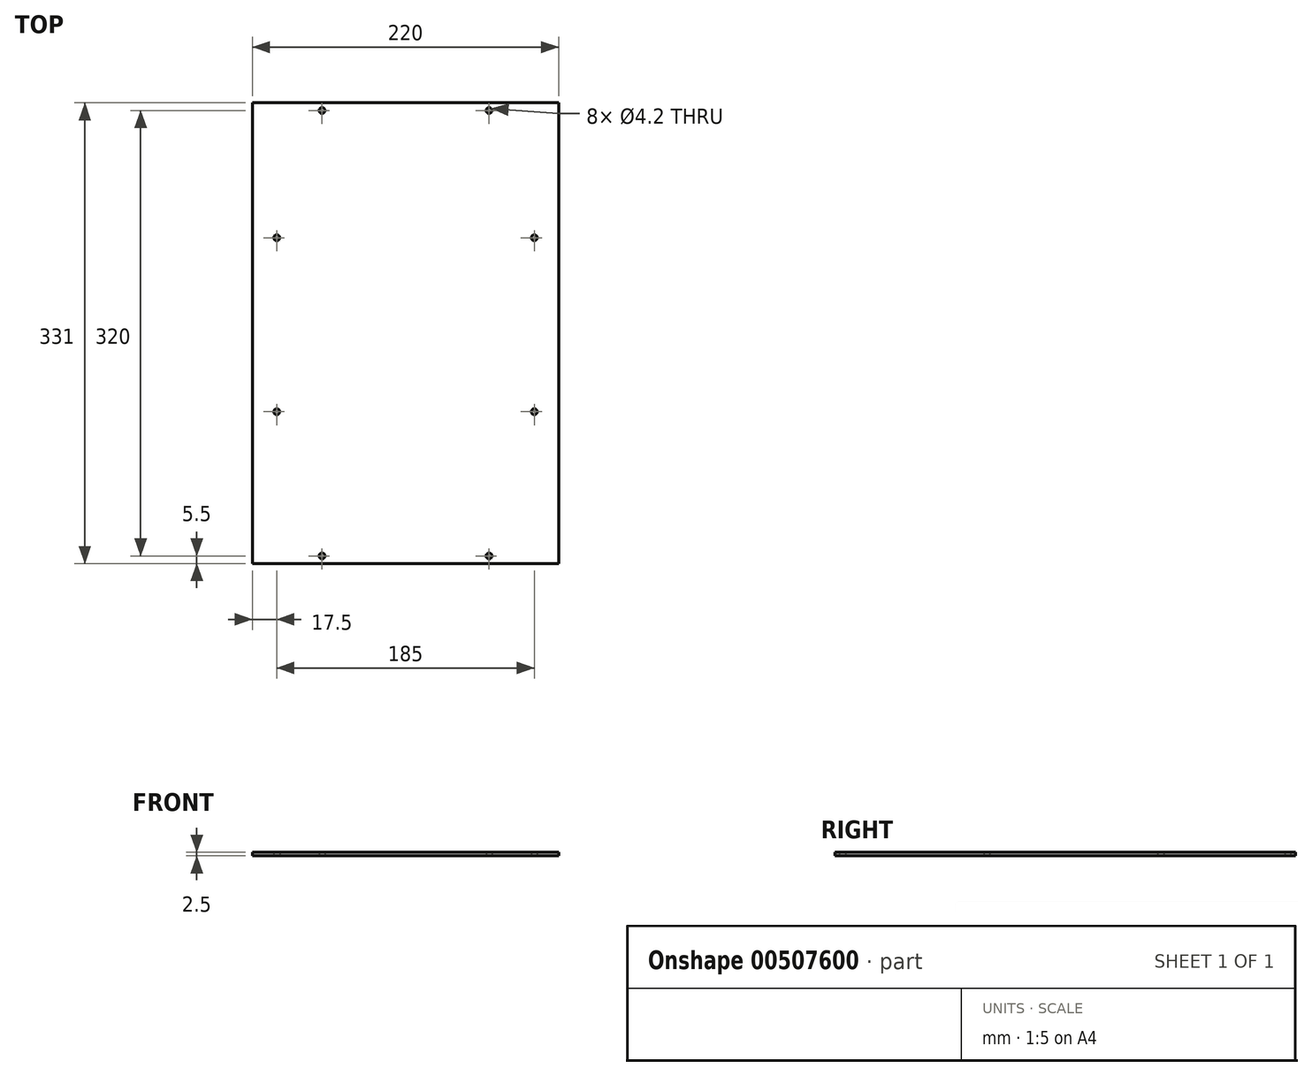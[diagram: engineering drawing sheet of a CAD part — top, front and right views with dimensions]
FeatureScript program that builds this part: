
annotation { "Feature Type Name" : "Feature", "Feature Type Description" : "" }
export const myFeature = defineFeature(function(context is Context, id is Id, definition is map)
    precondition{}
    {
        {
            var Q0;
            Q0=qCreatedBy(makeId("Top.planeOp"),FACE);
            var sketch = newSketch(context, id + "F0", { "sketchPlane" : qUnion([Q0])});
            skLineSegment(sketch, "E0.bottom", {"start": v(-110, 165.5) * mm, "end": v(110, 165.5) * mm});
            skLineSegment(sketch, "E0.top", {"start": v(-110, -165.5) * mm, "end": v(110, -165.5) * mm});
            skLineSegment(sketch, "E0.left", {"start": v(-110, 165.5) * mm, "end": v(-110, -165.5) * mm});
            skLineSegment(sketch, "E0.right", {"start": v(110, 165.5) * mm, "end": v(110, -165.5) * mm});
            skSolve(sketch);
        }
        {
            var Q0;
            Q0=makeQuery(id+"F0.imprint","IMPRINT",FACE,{"disambiguationData":[TD([[makeQuery(id+"F0.imprint","IMPRINT",EDGE,{"derivedFrom":sQuery(id+"F0.wireOp",EDGE,"E0.bottom")}),-1.0]])]});
            var sketch = newSketch(context, id + "F1", { "sketchPlane" : qUnion([Q0])});
            skCircle(sketch, "E1", {"center": v(-60, 160) * mm, "radius": 2.1 * mm});
            skCircle(sketch, "E2.MirrorC", {"center": v(60, 160) * mm, "radius": 2.1 * mm});
            skCircle(sketch, "E3.MirrorC", {"center": v(-60, -160) * mm, "radius": 2.1 * mm});
            skCircle(sketch, "E4.MirrorC", {"center": v(60, -160) * mm, "radius": 2.1 * mm});
            skCircle(sketch, "E5", {"center": v(92.5, 68.6) * mm, "radius": 2.1 * mm});
            skCircle(sketch, "E6", {"center": v(92.5, -56.4) * mm, "radius": 2.1 * mm});
            skCircle(sketch, "E7.MirrorC", {"center": v(-92.5, -56.4) * mm, "radius": 2.1 * mm});
            skCircle(sketch, "E8.MirrorC", {"center": v(-92.5, 68.6) * mm, "radius": 2.1 * mm});
            skSolve(sketch);
        }
        {
            var Q0;
            Q0 = qSketchRegion(id + "F0", true);
            extrude(context, id + "F2", {"entities" : qUnion([Q0]), "depth" : 2.5 * mm});
        }
        {
            var Q0;
            Q0=sQuery(id+"F1.wireOp",VERTEX,"E2.MirrorC.center");
            var Q1;
            Q1=sQuery(id+"F1.wireOp",VERTEX,"E1.center");
            var Q2;
            Q2=sQuery(id+"F1.wireOp",VERTEX,"E8.MirrorC.center");
            var Q3;
            Q3=sQuery(id+"F1.wireOp",VERTEX,"E5.center");
            var Q4;
            Q4=sQuery(id+"F1.wireOp",VERTEX,"E6.center");
            var Q5;
            Q5=sQuery(id+"F1.wireOp",VERTEX,"E7.MirrorC.center");
            var Q6;
            Q6=sQuery(id+"F1.wireOp",VERTEX,"E3.MirrorC.center");
            var Q7;
            Q7=sQuery(id+"F1.wireOp",VERTEX,"E4.MirrorC.center");
            var Q8;
            Q8=makeQuery(id+"F2.opExtrude","SWEPT_BODY",BODY,{"disambiguationData":[OSD([sQuery(id+"F0.wireOp",EDGE,"E0.bottom"),sQuery(id+"F0.wireOp",EDGE,"E0.top"),sQuery(id+"F0.wireOp",EDGE,"E0.left"),sQuery(id+"F0.wireOp",EDGE,"E0.right")])]});
            hole(context, id + "F3", {"style" : HoleStyle.SIMPLE, "endStyle" : HoleEndStyle.BLIND, "oppositeDirection" : true, "standardTappedOrClearance" : lookupTablePath({ "standard" : "ISO", "size" : "4.2", "type" : "Drilled" }), "standardBlindInLast" : lookupTablePath({ "standard" : "ISO", "size" : "4.2", "type" : "Drilled" }), "holeDiameter" : 4.2 * mm, "holeDepth" : 2.5 * mm, "isTappedThrough" : true, "tappedDepth" : 12 * mm, "tapClearance" : 3, "locations" : qUnion([Q0, Q1, Q2, Q3, Q4, Q5, Q6, Q7]), "scope" : qUnion([Q8])});
        }
    });
